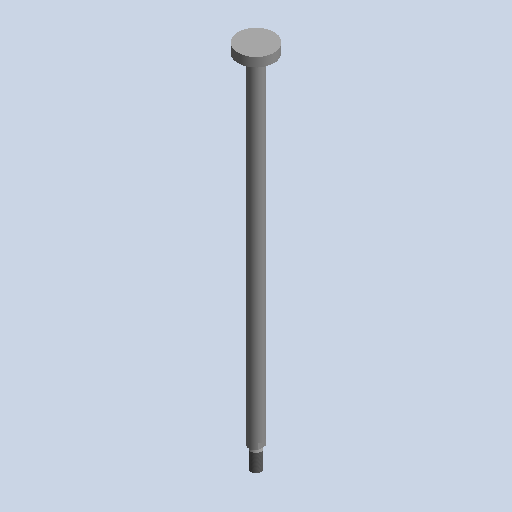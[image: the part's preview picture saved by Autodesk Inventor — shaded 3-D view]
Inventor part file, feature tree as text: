
AUTODESK INVENTOR PART (.ipt)
format: ipt  version: 2022 (Build 260153000, 153)  size: 131,584 bytes
history: native  units: mm (DEFAULTED — no unit token found)
features: other x28, sketch x3, revolve x2, thread x1, extrude x1
ambient origin geometry x8: Origin, YZ Plane, XZ Plane, XY Plane, X Axis, Y Axis, Z Axis, Center Point
bodies: Solid1 (feature_tree)
feature tree (35):
  revolve  "Revolution1"  Angle=360.0deg
  revolve  "Revolution2"  [1 undecoded]
  thread  "Thread1"  [1 undecoded]
  extrude  "Extrusion1"  [1 undecoded]
  other  "FDT_KSAUFSATZ_XY"
  other  "FDT_KSAUFSATZ_YZ"
  other  "FDT_KSAUFSATZ_ZX"
  other  "FDT_KSAUFSATZ_X"
  other  "FDT_KSAUFSATZ_Y"
  other  "FDT_KSAUFSATZ_Z"
  other  "FDT_KSAUFSATZ_Center"
  other  "FDT_NUT_XY"
  other  "FDT_NUT_YZ"
  other  "FDT_NUT_ZX"
  other  "FDT_NUT_X"
  other  "FDT_NUT_Y"
  other  "FDT_NUT_Z"
  other  "FDT_NUT_Center"
  other  "KS_XY"
  other  "KS_YZ"
  other  "KS_ZX"
  other  "KS_X"
  other  "KS_Y"
  other  "KS_Z"
  other  "KS_Center"
  other  "NUT1_XY"
  other  "NUT1_YZ"
  other  "NUT1_ZX"
  other  "NUT1_X"
  other  "NUT1_Y"
  other  "NUT1_Z"
  other  "NUT1_Center"
  sketch  "Sketch_2"  dims[d0=360.0deg d1=360.0deg]
  sketch  "Sketch_6"  dims[d2=19.2603mm d3=0.0mm d4=7.5mm d5=0.0mm]
  sketch  "Sketch_7"
note: 3 required parameter values undecoded (feature->parameter linkage not recoverable at this tier; creation-order binding heuristic only, values carry confidence <= 0.55)